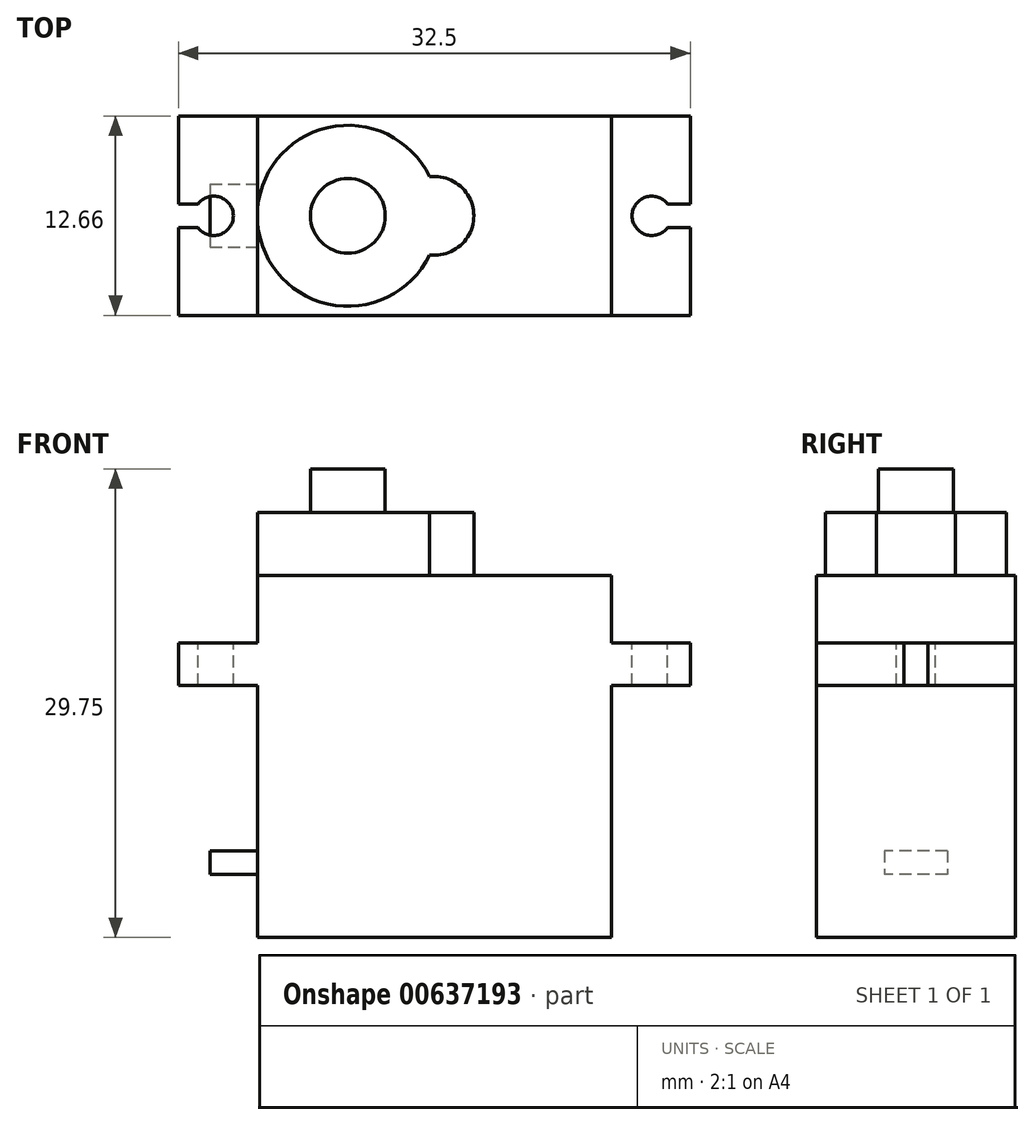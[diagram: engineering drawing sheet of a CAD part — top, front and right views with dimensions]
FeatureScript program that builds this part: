
annotation { "Feature Type Name" : "Feature", "Feature Type Description" : "" }
export const myFeature = defineFeature(function(context is Context, id is Id, definition is map)
    precondition{}
    {
        {
            var Q0;
            Q0=qCreatedBy(makeId("Top.planeOp"),FACE);
            var sketch = newSketch(context, id + "F0", { "sketchPlane" : qUnion([Q0])});
            skLineSegment(sketch, "E0.bottom", {"start": v(-11.25, 6.33) * mm, "end": v(11.25, 6.33) * mm});
            skLineSegment(sketch, "E0.top", {"start": v(-11.25, -6.33) * mm, "end": v(11.25, -6.33) * mm});
            skLineSegment(sketch, "E0.left", {"start": v(-11.25, 6.33) * mm, "end": v(-11.25, -6.33) * mm});
            skLineSegment(sketch, "E0.right", {"start": v(11.25, 6.33) * mm, "end": v(11.25, -6.32) * mm});
            skPoint(sketch, "E0.middle", {"position": v(0, 0) * mm});
            skSolve(sketch);
        }
        {
            var Q0;
            Q0=makeQuery(id+"F0.imprint","IMPRINT",FACE,{"disambiguationData":[TD([[makeQuery(id+"F0.imprint","IMPRINT",EDGE,{"derivedFrom":sQuery(id+"F0.wireOp",EDGE,"E0.bottom")}),-1.0]])]});
            extrude(context, id + "F1", {"entities" : qUnion([Q0]), "depth" : 23 * mm, "offsetDistance" : 25 * mm});
        }
        {
            var Q0;
            Q0=makeQuery(id+"F1.opExtrude","SWEPT_FACE",FACE,{"disambiguationData":[OSD([sQuery(id+"F0.wireOp",EDGE,"E0.left")])]});
            var sketch = newSketch(context, id + "F2", { "sketchPlane" : qUnion([Q0])});
            skLineSegment(sketch, "E1.bottom", {"start": v(-6.32, 18.7) * mm, "end": v(6.33, 18.7) * mm});
            skLineSegment(sketch, "E1.top", {"start": v(-6.32, 16) * mm, "end": v(6.33, 16) * mm});
            skLineSegment(sketch, "E1.left", {"start": v(-6.32, 18.7) * mm, "end": v(-6.32, 16) * mm});
            skLineSegment(sketch, "E1.right", {"start": v(6.33, 18.7) * mm, "end": v(6.33, 16) * mm});
            skSolve(sketch);
        }
        {
            var Q0;
            Q0=makeQuery(id+"F2.imprint","IMPRINT",FACE,{"disambiguationData":[TD([[makeQuery(id+"F2.imprint","IMPRINT",EDGE,{"derivedFrom":sQuery(id+"F2.wireOp",EDGE,"E1.bottom")}),-1.0]])]});
            extrude(context, id + "F3", {"entities" : qUnion([Q0]), "operationType" : NewBodyOperationType.ADD, "depth" : 5 * mm, "offsetDistance" : 25 * mm});
        }
        {
            var Q0;
            {var subQ1=sQuery(id+"F0.wireOp",EDGE,"E0.left");Q0=makeQuery(id+"F3.boolean.opBoolean","SPLIT",FACE,{"disambiguationData":[TD([makeQuery(id+"F3.opExtrude","SWEPT_FACE",FACE,{"disambiguationData":[OSD([sQuery(id+"F2.wireOp",EDGE,"E1.top")])]})])],"derivedFrom":makeQuery(id+"F1.opExtrude","SWEPT_FACE",FACE,{"disambiguationData":[OSD([subQ1])]})});}
            var sketch = newSketch(context, id + "F4", { "sketchPlane" : qUnion([Q0])});
            skLineSegment(sketch, "E2.bottom", {"start": v(-2, 5.5) * mm, "end": v(2, 5.5) * mm});
            skLineSegment(sketch, "E2.top", {"start": v(-2, 4) * mm, "end": v(2, 4) * mm});
            skLineSegment(sketch, "E2.left", {"start": v(-2, 5.5) * mm, "end": v(-2, 4) * mm});
            skLineSegment(sketch, "E2.right", {"start": v(2, 5.5) * mm, "end": v(2, 4) * mm});
            skPoint(sketch, "E2.middle", {"position": v(0, 8) * mm});
            skPoint(sketch, "E2.middle.positionSnap0", {"position": v(-6.32, 8) * mm});
            skPoint(sketch, "E2.centerSnap0", {"position": v(-6.32, 8) * mm});
            skSolve(sketch);
        }
        {
            var Q0;
            Q0=makeQuery(id+"F4.imprint","IMPRINT",FACE,{"disambiguationData":[TD([[makeQuery(id+"F4.imprint","IMPRINT",EDGE,{"derivedFrom":sQuery(id+"F4.wireOp",EDGE,"E2.bottom")}),-1.0]])]});
            extrude(context, id + "F5", {"entities" : qUnion([Q0]), "operationType" : NewBodyOperationType.ADD, "depth" : 3 * mm, "offsetDistance" : 25 * mm});
        }
        {
            var Q0;
            Q0=makeQuery(id+"F3.opExtrude","SWEPT_FACE",FACE,{"disambiguationData":[OSD([sQuery(id+"F2.wireOp",EDGE,"E1.bottom")])]});
            var sketch = newSketch(context, id + "F6", { "sketchPlane" : qUnion([Q0])});
            skCircle(sketch, "E3", {"center": v(-14.02, 0) * mm, "radius": 1.25 * mm});
            skPoint(sketch, "E3.centerSnap0", {"position": v(-11.25, 0) * mm});
            skSolve(sketch);
        }
        {
            var Q0;
            Q0=makeQuery(id+"F6.imprint","IMPRINT",FACE,{"disambiguationData":[TD([[makeQuery(id+"F6.imprint","IMPRINT",EDGE,{"derivedFrom":sQuery(id+"F6.wireOp",EDGE,"E3")}),1.0]])]});
            extrude(context, id + "F7", {"entities" : qUnion([Q0]), "operationType" : NewBodyOperationType.REMOVE, "endBound" : BoundingType.UP_TO_NEXT, "oppositeDirection" : true, "depth" : 25 * mm, "offsetDistance" : 25 * mm});
        }
        {
            var Q0;
            Q0=makeQuery(id+"F1.opExtrude","SWEPT_FACE",FACE,{"disambiguationData":[OSD([sQuery(id+"F0.wireOp",EDGE,"E0.right")])]});
            var sketch = newSketch(context, id + "F8", { "sketchPlane" : qUnion([Q0])});
            skLineSegment(sketch, "E4.bottom", {"start": v(-6.32, 18.7) * mm, "end": v(6.33, 18.7) * mm});
            skLineSegment(sketch, "E4.top", {"start": v(-6.32, 16) * mm, "end": v(6.33, 16) * mm});
            skLineSegment(sketch, "E4.left", {"start": v(-6.32, 18.7) * mm, "end": v(-6.32, 16) * mm});
            skLineSegment(sketch, "E4.right", {"start": v(6.33, 18.7) * mm, "end": v(6.33, 16) * mm});
            skSolve(sketch);
        }
        {
            var Q0;
            Q0=makeQuery(id+"F8.imprint","IMPRINT",FACE,{"disambiguationData":[TD([[makeQuery(id+"F8.imprint","IMPRINT",EDGE,{"derivedFrom":sQuery(id+"F8.wireOp",EDGE,"E4.bottom")}),-1.0]])]});
            extrude(context, id + "F9", {"entities" : qUnion([Q0]), "operationType" : NewBodyOperationType.ADD, "depth" : 5 * mm, "offsetDistance" : 25 * mm});
        }
        {
            var Q0;
            Q0=makeQuery(id+"F9.opExtrude","SWEPT_FACE",FACE,{"disambiguationData":[OSD([sQuery(id+"F8.wireOp",EDGE,"E4.bottom")])]});
            var sketch = newSketch(context, id + "F10", { "sketchPlane" : qUnion([Q0])});
            skCircle(sketch, "E5", {"center": v(13.8, 0) * mm, "radius": 1.25 * mm});
            skSolve(sketch);
        }
        {
            var Q0;
            Q0=makeQuery(id+"F10.imprint","IMPRINT",FACE,{"disambiguationData":[TD([[makeQuery(id+"F10.imprint","IMPRINT",EDGE,{"derivedFrom":sQuery(id+"F10.wireOp",EDGE,"E5")}),1.0]])]});
            extrude(context, id + "F11", {"entities" : qUnion([Q0]), "operationType" : NewBodyOperationType.REMOVE, "endBound" : BoundingType.UP_TO_NEXT, "oppositeDirection" : true, "depth" : 25 * mm, "offsetDistance" : 25 * mm});
        }
        {
            var Q0;
            Q0=makeQuery(id+"F1.opExtrude","CAP_FACE",FACE,{"disambiguationData":[OSD([sQuery(id+"F0.wireOp",EDGE,"E0.bottom"),sQuery(id+"F0.wireOp",EDGE,"E0.top"),sQuery(id+"F0.wireOp",EDGE,"E0.left"),sQuery(id+"F0.wireOp",EDGE,"E0.right")])],"isStart":false});
            var sketch = newSketch(context, id + "F12", { "sketchPlane" : qUnion([Q0])});
            skPoint(sketch, "E6.centerSnap0", {"position": v(-11.25, 0) * mm});
            skArc(sketch, "E7", {"start": v(-0.31, 2.48) * mm, "mid": v(-11.25, 0) * mm, "end": v(-0.31, -2.48) * mm});
            skArc(sketch, "E8", {"start": v(-0.31, -2.48) * mm, "mid": v(2.5, 0) * mm, "end": v(-0.31, 2.48) * mm});
            skCircle(sketch, "E9", {"center": v(-5.5, 0) * mm, "radius": 2.38 * mm});
            skSolve(sketch);
        }
        {
            var Q0;
            Q0=makeQuery(id+"F12.imprint","IMPRINT",FACE,{"disambiguationData":[TD([[makeQuery(id+"F12.imprint","IMPRINT",EDGE,{"derivedFrom":sQuery(id+"F12.wireOp",EDGE,"E7")}),1.0]])]});
            var Q1;
            Q1=makeQuery(id+"F12.imprint","IMPRINT",FACE,{"disambiguationData":[TD([[makeQuery(id+"F12.imprint","IMPRINT",EDGE,{"derivedFrom":sQuery(id+"F12.wireOp",EDGE,"E9")}),1.0]])]});
            extrude(context, id + "F13", {"entities" : qUnion([Q0, Q1]), "operationType" : NewBodyOperationType.ADD, "depth" : 4 * mm, "offsetDistance" : 25 * mm});
        }
        {
            var Q0;
            Q0=makeQuery(id+"F13.opExtrude","CAP_FACE",FACE,{"disambiguationData":[OSD([sQuery(id+"F12.wireOp",EDGE,"E7"),sQuery(id+"F12.wireOp",EDGE,"E8")])],"isStart":false});
            var sketch = newSketch(context, id + "F14", { "sketchPlane" : qUnion([Q0])});
            skCircle(sketch, "E10", {"center": v(-5.5, 0) * mm, "radius": 2.38 * mm});
            skSolve(sketch);
        }
        {
            var Q0;
            Q0=makeQuery(id+"F14.imprint","IMPRINT",FACE,{"disambiguationData":[TD([[makeQuery(id+"F14.imprint","IMPRINT",EDGE,{"derivedFrom":sQuery(id+"F14.wireOp",EDGE,"E10")}),1.0]])]});
            extrude(context, id + "F15", {"entities" : qUnion([Q0]), "operationType" : NewBodyOperationType.ADD, "depth" : 2.75 * mm, "offsetDistance" : 25 * mm});
        }
        {
            var Q0;
            Q0=makeQuery(id+"F9.opExtrude","SWEPT_FACE",FACE,{"disambiguationData":[OSD([sQuery(id+"F8.wireOp",EDGE,"E4.bottom")])]});
            var sketch = newSketch(context, id + "F16", { "sketchPlane" : qUnion([Q0])});
            skLineSegment(sketch, "E11.bottom", {"start": v(14.8, 0.75) * mm, "end": v(16.8, 0.75) * mm});
            skLineSegment(sketch, "E11.top", {"start": v(14.8, -0.75) * mm, "end": v(16.8, -0.75) * mm});
            skLineSegment(sketch, "E11.left", {"start": v(14.8, 0.75) * mm, "end": v(14.8, -0.75) * mm});
            skLineSegment(sketch, "E11.right", {"start": v(16.8, 0.75) * mm, "end": v(16.8, -0.75) * mm});
            skPoint(sketch, "E11.middle", {"position": v(15.8, 0) * mm});
            skSolve(sketch);
        }
        {
            var Q0;
            {var subQ1=sQuery(id+"F16.wireOp",EDGE,"E11.bottom");var subQ4=makeQuery(id+"F9.opExtrude","CAP_EDGE",EDGE,{"disambiguationData":[OSD([sQuery(id+"F8.wireOp",EDGE,"E4.bottom")])],"isStart":false});var subQ5=makeQuery(id+"F16.imprint","INTERSECT",VERTEX,{"derivedFrom":[subQ4,subQ1]});Q0=makeQuery(id+"F16.imprint","IMPRINT",FACE,{"disambiguationData":[TD([[makeQuery(id+"F16.imprint","IMPRINT",EDGE,{"disambiguationData":[TD([[subQ5,1.0]])],"derivedFrom":subQ4}),1.0]])]});}
            extrude(context, id + "F17", {"entities" : qUnion([Q0]), "operationType" : NewBodyOperationType.REMOVE, "endBound" : BoundingType.UP_TO_NEXT, "oppositeDirection" : true, "depth" : 25 * mm, "offsetDistance" : 25 * mm});
        }
        {
            var Q0;
            Q0=makeQuery(id+"F3.opExtrude","SWEPT_FACE",FACE,{"disambiguationData":[OSD([sQuery(id+"F2.wireOp",EDGE,"E1.bottom")])]});
            var sketch = newSketch(context, id + "F18", { "sketchPlane" : qUnion([Q0])});
            skLineSegment(sketch, "E12.bottom", {"start": v(-16.98, 0.75) * mm, "end": v(-14.67, 0.75) * mm});
            skLineSegment(sketch, "E12.top", {"start": v(-16.98, -0.75) * mm, "end": v(-14.67, -0.75) * mm});
            skLineSegment(sketch, "E12.left", {"start": v(-16.98, 0.75) * mm, "end": v(-16.98, -0.75) * mm});
            skLineSegment(sketch, "E12.right", {"start": v(-14.67, 0.75) * mm, "end": v(-14.67, -0.75) * mm});
            skPoint(sketch, "E12.middle", {"position": v(-15.83, 0) * mm});
            skSolve(sketch);
        }
        {
            var Q0;
            {var subQ0=sQuery(id+"F18.wireOp",EDGE,"E12.bottom");var subQ1=makeQuery(id+"F3.opExtrude","CAP_EDGE",EDGE,{"disambiguationData":[OSD([sQuery(id+"F2.wireOp",EDGE,"E1.bottom")])],"isStart":false});var subQ2=makeQuery(id+"F18.imprint","INTERSECT",VERTEX,{"derivedFrom":[subQ1,subQ0]});Q0=makeQuery(id+"F18.imprint","IMPRINT",FACE,{"disambiguationData":[TD([[makeQuery(id+"F18.imprint","IMPRINT",EDGE,{"disambiguationData":[TD([[subQ2,-1.0]])],"derivedFrom":subQ0}),-1.0]])]});}
            extrude(context, id + "F19", {"entities" : qUnion([Q0]), "operationType" : NewBodyOperationType.REMOVE, "endBound" : BoundingType.UP_TO_NEXT, "oppositeDirection" : true, "depth" : 25 * mm, "offsetDistance" : 25 * mm});
        }
    });
